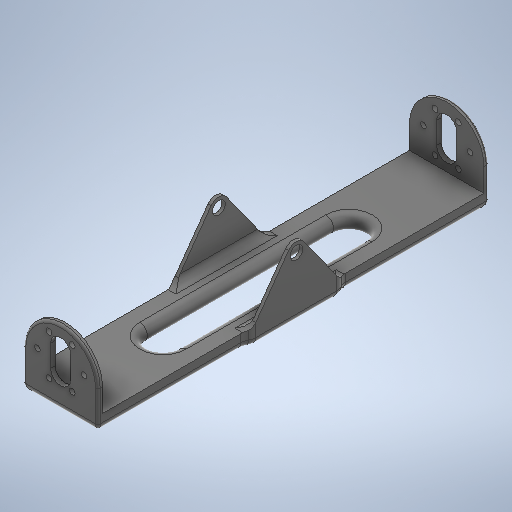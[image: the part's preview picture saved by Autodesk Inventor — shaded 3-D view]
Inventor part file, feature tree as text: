
AUTODESK INVENTOR PART (.ipt)
format: ipt  version: 2025.2 (Build 292293000, 293)  size: 638,976 bytes
history: native  units: mm
features: sketch x10, extrude x8, fillet x6, projected_geometry x3, plane x2, mirror x2
ambient origin geometry x8: Origin, YZ Plane, XZ Plane, XY Plane, X Axis, Y Axis, Z Axis, Center Point
bodies: Solid1 (feature_tree)
feature tree (31):
  extrude  "Extrusion1"  Depth=250.0mm
  extrude  "Extrusion2"  Depth=2.0mm TaperAngle=0.0deg
  extrude  "Extrusion4"  TaperAngle=90.0deg  [1 undecoded]
  sketch  "Sketch6"  dims[d83=3.75mm d84=60.0mm d86=360.0deg]
  plane  "Work Plane5"
  plane  "Work Plane6"
  mirror  "Mirror5"
  mirror  "Mirror6"
  fillet  "Fillet12"  Radius=48.0mm
  fillet  "Fillet13"  Radius=39.0mm
  fillet  "Fillet14"  [1 undecoded]
  fillet  "Fillet15"  Radius=14.0mm
  extrude  "Extrusion5"  Depth=13.0mm
  extrude  "Extrusion6"  Depth=60.0mm TaperAngle=360.0deg
  extrude  "Extrusion7"  Depth=60.0mm
  extrude  "Extrusion8"  Depth=8.0mm
  extrude  "Extrusion9"  Depth=8.0mm
  fillet  "Fillet17"  Radius=8.0mm
  fillet  "Fillet18"  Radius=8.0mm
  sketch  "Sketch1"  dims[d0=48.0mm d1=250.0mm]
  sketch  "Sketch2"  dims[d2=2.0mm d3=0.0mm d6=2.0mm d7=0.0mm]
  sketch  "Sketch5"  dims[d81=90.0deg d82=13.0mm]
  sketch  "Sketch Circular Pattern4"  dims[d67=2.0mm d68=0.0mm d69=90.0deg d77=48.0mm d78=39.0mm d79=180.0deg d80=14.0mm]
  sketch  "Sketch7"  dims[d89=90.0deg d91=60.0mm]
  projected_geometry  "Projected Loop1"
  sketch  "Sketch8"  dims[d92=2.0mm d93=8.0mm]
  projected_geometry  "Projected Loop2"
  sketch  "Sketch10"  dims[d94=12.25mm d95=8.0mm d96=8.0mm d97=8.0mm]
  sketch  "Sketch11"  dims[d98=5.0mm]
  sketch  "Sketch12"  dims[d99=1.0mm d100=0.0mm d101=1.0mm d102=0.0mm d103=8.3mm d104=0.0mm d105=0.0mm d107=60.0mm d108=20.0mm d109=10.0mm d110=0.0mm d111=8.0mm d112=0.0mm d113=1.5mm d114=5.0mm d75=0.5mm d76=0.872665mm d106=0.872665mm]
  projected_geometry  "Projected Loop4"
note: 2 required parameter values undecoded (feature->parameter linkage not recoverable at this tier; creation-order binding heuristic only, values carry confidence <= 0.55)
